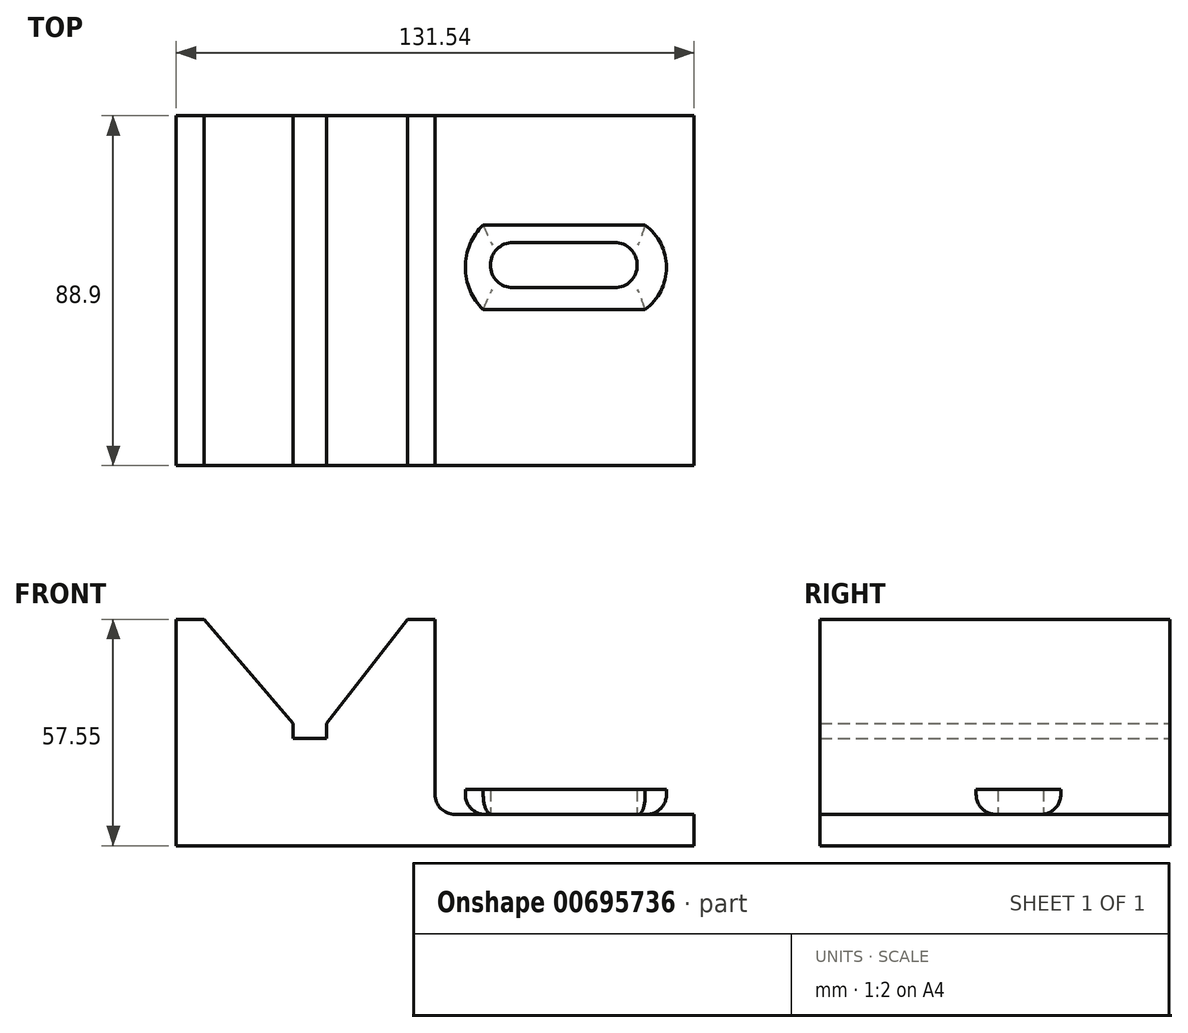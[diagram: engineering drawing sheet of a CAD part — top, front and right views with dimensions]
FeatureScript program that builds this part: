
annotation { "Feature Type Name" : "Feature", "Feature Type Description" : "" }
export const myFeature = defineFeature(function(context is Context, id is Id, definition is map)
    precondition{}
    {
        {
            var Q0;
            Q0=qCreatedBy(makeId("Front.planeOp"),FACE);
            var sketch = newSketch(context, id + "F0", { "sketchPlane" : qUnion([Q0])});
            skLineSegment(sketch, "E0", {"start": v(-71.5, -39.05) * mm, "end": v(60.04, -39.05) * mm});
            skLineSegment(sketch, "E1", {"start": v(60.04, -39.05) * mm, "end": v(60.04, -31.12) * mm});
            skLineSegment(sketch, "E2", {"start": v(60.04, -31.12) * mm, "end": v(-5.73, -31.12) * mm});
            skLineSegment(sketch, "E3", {"start": v(-5.73, -31.12) * mm, "end": v(-5.73, 18.5) * mm});
            skLineSegment(sketch, "E4", {"start": v(-5.73, 18.5) * mm, "end": v(-12.77, 18.5) * mm});
            skLineSegment(sketch, "E5", {"start": v(-12.77, 18.5) * mm, "end": v(-33.33, -7.93) * mm});
            skLineSegment(sketch, "E6", {"start": v(-33.33, -7.93) * mm, "end": v(-33.33, -11.74) * mm});
            skLineSegment(sketch, "E7", {"start": v(-33.33, -11.74) * mm, "end": v(-41.84, -11.74) * mm});
            skLineSegment(sketch, "E8", {"start": v(-41.84, -11.74) * mm, "end": v(-41.84, -7.93) * mm});
            skLineSegment(sketch, "E9", {"start": v(-41.84, -7.93) * mm, "end": v(-64.45, 18.5) * mm});
            skLineSegment(sketch, "E10", {"start": v(-64.45, 18.5) * mm, "end": v(-71.5, 18.5) * mm});
            skLineSegment(sketch, "E11", {"start": v(-71.5, 18.5) * mm, "end": v(-71.5, -39.05) * mm});
            skSolve(sketch);
        }
        {
            var Q0;
            Q0 = qSketchRegion(id + "F0", true);
            extrude(context, id + "F1", {"entities" : qUnion([Q0]), "depth" : 88.9 * mm, "offsetDistance" : 25.4 * mm});
        }
        {
            var Q0;
            Q0=makeQuery(id+"F1.opExtrude","SWEPT_FACE",FACE,{"disambiguationData":[OSD([sQuery(id+"F0.wireOp",EDGE,"E2")])]});
            var sketch = newSketch(context, id + "F2", { "sketchPlane" : qUnion([Q0])});
            skLineSegment(sketch, "E12", {"start": v(14.05, -32.2) * mm, "end": v(39.87, -32.2) * mm});
            skLineSegment(sketch, "E13", {"start": v(14.05, -43.68) * mm, "end": v(39.87, -43.68) * mm});
            skLineSegment(sketch, "E14", {"start": v(6.47, -49.23) * mm, "end": v(47.64, -49.23) * mm});
            skArc(sketch, "E15", {"start": v(39.87, -43.68) * mm, "mid": v(45.6, -37.94) * mm, "end": v(39.87, -32.2) * mm});
            skArc(sketch, "E16", {"start": v(14.05, -32.2) * mm, "mid": v(8.3, -37.94) * mm, "end": v(14.05, -43.68) * mm});
            skPoint(sketch, "E17.end.orphan", {"position": v(47.64, -23.99) * mm});
            skPoint(sketch, "E17.start.orphan", {"position": v(6.47, -23.99) * mm});
            skLineSegment(sketch, "E18", {"start": v(6.47, -27.73) * mm, "end": v(47.64, -27.73) * mm});
            skArc(sketch, "E19", {"start": v(47.64, -49.23) * mm, "mid": v(53.03, -38.48) * mm, "end": v(47.64, -27.73) * mm});
            skArc(sketch, "E20", {"start": v(6.47, -27.73) * mm, "mid": v(1.93, -38.48) * mm, "end": v(6.47, -49.23) * mm});
            skSolve(sketch);
        }
        {
            var Q0;
            Q0 = qSketchRegion(id + "F2", true);
            extrude(context, id + "F3", {"entities" : qUnion([Q0]), "depth" : 6.35 * mm, "offsetDistance" : 25.4 * mm});
        }
        {
            var Q0;
            Q0=makeQuery(id+"F1.opExtrude","SWEPT_EDGE",EDGE,{"disambiguationData":[OSD([sQuery(id+"F0.wireOp",EDGE,"E2"),sQuery(id+"F0.wireOp",EDGE,"E3")])]});
            var Q1;
            Q1=makeQuery(id+"F3.opExtrude","CAP_EDGE",EDGE,{"disambiguationData":[OSD([sQuery(id+"F2.wireOp",EDGE,"E14")])],"isStart":true});
            var Q2;
            Q2=makeQuery(id+"F3.opExtrude","CAP_EDGE",EDGE,{"disambiguationData":[OSD([sQuery(id+"F2.wireOp",EDGE,"E19")])],"isStart":true});
            var Q3;
            Q3=makeQuery(id+"F3.opExtrude","CAP_EDGE",EDGE,{"disambiguationData":[OSD([sQuery(id+"F2.wireOp",EDGE,"E18")])],"isStart":true});
            var Q4;
            Q4=makeQuery(id+"F3.opExtrude","CAP_EDGE",EDGE,{"disambiguationData":[OSD([sQuery(id+"F2.wireOp",EDGE,"E20")])],"isStart":true});
            fillet(context, id + "F4", {"entities" : qUnion([Q0, Q1, Q2, Q3, Q4]), "radius" : 5.08 * mm, "tangentPropagation" : true, "allowEdgeOverflow" : false});
        }
    });
